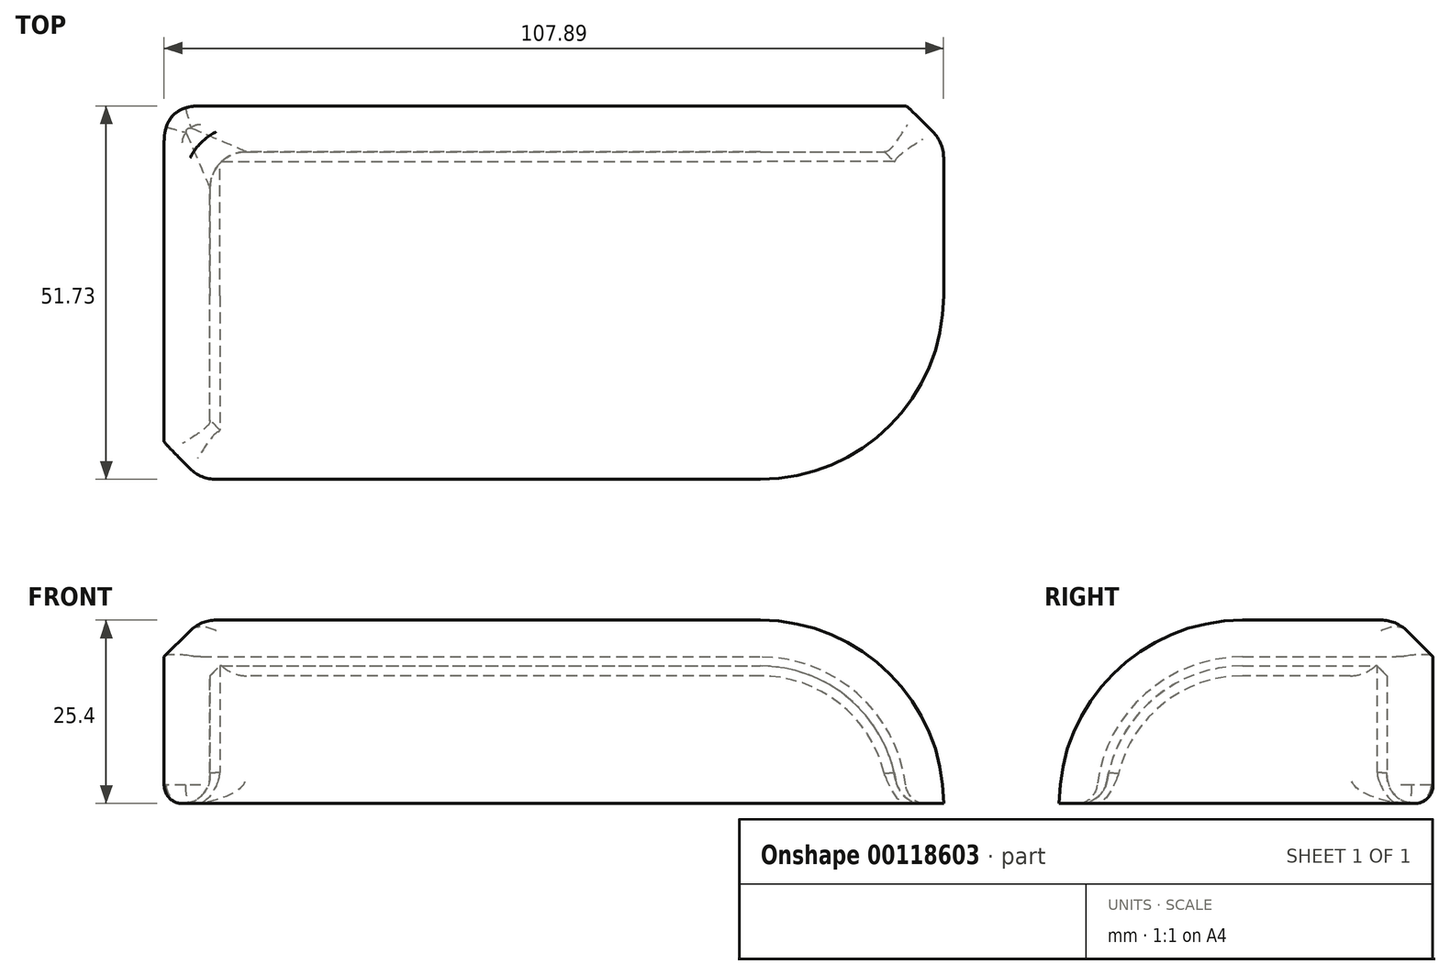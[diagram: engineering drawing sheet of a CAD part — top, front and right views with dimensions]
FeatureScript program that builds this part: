
annotation { "Feature Type Name" : "Feature", "Feature Type Description" : "" }
export const myFeature = defineFeature(function(context is Context, id is Id, definition is map)
    precondition{}
    {
        {
            var Q0;
            Q0=qCreatedBy(makeId("Top.planeOp"),FACE);
            var sketch = newSketch(context, id + "F0", { "sketchPlane" : qUnion([Q0])});
            skLineSegment(sketch, "E0.bottom", {"start": v(-60.63, -3.39) * mm, "end": v(47.26, -3.39) * mm});
            skLineSegment(sketch, "E0.top", {"start": v(-60.63, 48.34) * mm, "end": v(47.26, 48.34) * mm});
            skLineSegment(sketch, "E0.left", {"start": v(-60.63, -3.39) * mm, "end": v(-60.63, 48.34) * mm});
            skLineSegment(sketch, "E0.right", {"start": v(47.26, -3.39) * mm, "end": v(47.26, 48.34) * mm});
            skSolve(sketch);
        }
        {
            var Q0;
            Q0=makeQuery(id+"F0.imprint","IMPRINT",FACE,{"disambiguationData":[TD([[makeQuery(id+"F0.imprint","IMPRINT",EDGE,{"derivedFrom":sQuery(id+"F0.wireOp",EDGE,"E0.bottom")}),1.0]])]});
            extrude(context, id + "F1", {"entities" : qUnion([Q0]), "depth" : 25.4 * mm});
        }
        {
            var Q0;
            Q0=makeQuery(id+"F1.opExtrude","CAP_EDGE",EDGE,{"disambiguationData":[OSD([sQuery(id+"F0.wireOp",EDGE,"E0.bottom")])],"isStart":false});
            var Q1;
            Q1=makeQuery(id+"F1.opExtrude","CAP_EDGE",EDGE,{"disambiguationData":[OSD([sQuery(id+"F0.wireOp",EDGE,"E0.right")])],"isStart":false});
            var Q2;
            Q2=makeQuery(id+"F1.opExtrude","SWEPT_EDGE",EDGE,{"disambiguationData":[OSD([sQuery(id+"F0.wireOp",EDGE,"E0.bottom"),sQuery(id+"F0.wireOp",EDGE,"E0.right")])]});
            fillet(context, id + "F2", {"entities" : qUnion([Q0, Q1, Q2]), "radius" : 25.4 * mm, "tangentPropagation" : true, "allowEdgeOverflow" : false});
        }
        {
            var Q0;
            Q0=makeQuery(id+"F2.opFillet","BLEND_EDGE",EDGE,{"blendedFrom":[makeQuery(id+"F1.opExtrude","CAP_EDGE",EDGE,{"disambiguationData":[OSD([sQuery(id+"F0.wireOp",EDGE,"E0.right")])],"isStart":false}),makeQuery(id+"F1.opExtrude","SWEPT_FACE",FACE,{"disambiguationData":[OSD([sQuery(id+"F0.wireOp",EDGE,"E0.top")])]})],"blendedInto":[makeQuery(id+"F1.opExtrude","SWEPT_FACE",FACE,{"disambiguationData":[OSD([sQuery(id+"F0.wireOp",EDGE,"E0.top")])]})]});
            var Q1;
            Q1=makeQuery(id+"F1.opExtrude","CAP_FACE",FACE,{"disambiguationData":[OSD([sQuery(id+"F0.wireOp",EDGE,"E0.bottom"),sQuery(id+"F0.wireOp",EDGE,"E0.top"),sQuery(id+"F0.wireOp",EDGE,"E0.left"),sQuery(id+"F0.wireOp",EDGE,"E0.right")])],"isStart":false});
            chamfer(context, id + "F3", {"entities" : qUnion([Q0, Q1]), "width" : 5.08 * mm, "tangentPropagation" : true});
        }
        {
            var Q0;
            Q0=makeQuery(id+"F1.opExtrude","CAP_FACE",FACE,{"disambiguationData":[OSD([sQuery(id+"F0.wireOp",EDGE,"E0.bottom"),sQuery(id+"F0.wireOp",EDGE,"E0.top"),sQuery(id+"F0.wireOp",EDGE,"E0.left"),sQuery(id+"F0.wireOp",EDGE,"E0.right")])],"isStart":true});
            shell(context, id + "F4", {"entities" : qUnion([Q0]), "thickness" : 6.35 * mm});
        }
        {
            var Q0;
            {var subQ0=sQuery(id+"F0.wireOp",EDGE,"E0.top");Q0=makeQuery(id+"F4.opShell","OFFSET_EDGE",EDGE,{"disambiguationData":[OSD([subQ0]),TDD([makeQuery(id+"F1.opExtrude","CAP_EDGE",EDGE,{"disambiguationData":[OSD([subQ0])],"isStart":true})])]});}
            var Q1;
            {var subQ0=sQuery(id+"F0.wireOp",EDGE,"E0.right");var subQ1=sQuery(id+"F0.wireOp",EDGE,"E0.left");var subQ2=sQuery(id+"F0.wireOp",EDGE,"E0.top");var subQ3=sQuery(id+"F0.wireOp",EDGE,"E0.bottom");Q1=makeQuery(id+"F4.opShell","OFFSET_EDGE",EDGE,{"disambiguationData":[OSD([subQ3,subQ2,subQ1,subQ0]),TDD([makeQuery(id+"F2.opFillet","BLEND_EDGE",EDGE,{"blendedFrom":[makeQuery(id+"F1.opExtrude","CAP_EDGE",EDGE,{"disambiguationData":[OSD([subQ0])],"isStart":false}),makeQuery(id+"F1.opExtrude","CAP_FACE",FACE,{"disambiguationData":[OSD([subQ3,subQ2,subQ1,subQ0])],"isStart":true})],"blendedInto":[makeQuery(id+"F1.opExtrude","CAP_FACE",FACE,{"disambiguationData":[OSD([subQ3,subQ2,subQ1,subQ0])],"isStart":true})]})])]});}
            var Q2;
            {var subQ0=sQuery(id+"F0.wireOp",EDGE,"E0.left");Q2=makeQuery(id+"F4.opShell","OFFSET_EDGE",EDGE,{"disambiguationData":[OSD([subQ0]),TDD([makeQuery(id+"F1.opExtrude","CAP_EDGE",EDGE,{"disambiguationData":[OSD([subQ0])],"isStart":true})])]});}
            var Q3;
            {var subQ0=sQuery(id+"F0.wireOp",EDGE,"E0.right");var subQ1=sQuery(id+"F0.wireOp",EDGE,"E0.left");var subQ2=sQuery(id+"F0.wireOp",EDGE,"E0.top");var subQ3=sQuery(id+"F0.wireOp",EDGE,"E0.bottom");Q3=makeQuery(id+"F4.opShell","OFFSET_EDGE",EDGE,{"disambiguationData":[OSD([subQ3,subQ2,subQ1,subQ0]),TDD([makeQuery(id+"F2.opFillet","BLEND_EDGE",EDGE,{"blendedFrom":[makeQuery(id+"F1.opExtrude","CAP_VERTEX",VERTEX,{"disambiguationData":[OSD([subQ3,subQ0])],"isStart":false}),makeQuery(id+"F1.opExtrude","CAP_FACE",FACE,{"disambiguationData":[OSD([subQ3,subQ2,subQ1,subQ0])],"isStart":true})],"blendedInto":[makeQuery(id+"F1.opExtrude","CAP_FACE",FACE,{"disambiguationData":[OSD([subQ3,subQ2,subQ1,subQ0])],"isStart":true})]})])]});}
            var Q4;
            {var subQ0=sQuery(id+"F0.wireOp",EDGE,"E0.right");var subQ1=sQuery(id+"F0.wireOp",EDGE,"E0.left");var subQ2=sQuery(id+"F0.wireOp",EDGE,"E0.top");var subQ3=sQuery(id+"F0.wireOp",EDGE,"E0.bottom");Q4=makeQuery(id+"F4.opShell","OFFSET_EDGE",EDGE,{"disambiguationData":[OSD([subQ3,subQ2,subQ1,subQ0]),TDD([makeQuery(id+"F2.opFillet","BLEND_EDGE",EDGE,{"blendedFrom":[makeQuery(id+"F1.opExtrude","CAP_EDGE",EDGE,{"disambiguationData":[OSD([subQ3])],"isStart":false}),makeQuery(id+"F1.opExtrude","CAP_FACE",FACE,{"disambiguationData":[OSD([subQ3,subQ2,subQ1,subQ0])],"isStart":true})],"blendedInto":[makeQuery(id+"F1.opExtrude","CAP_FACE",FACE,{"disambiguationData":[OSD([subQ3,subQ2,subQ1,subQ0])],"isStart":true})]})])]});}
            fillet(context, id + "F5", {"entities" : qUnion([Q0, Q1, Q2, Q3, Q4]), "radius" : 3.8 * mm, "tangentPropagation" : true, "allowEdgeOverflow" : false});
        }
        {
            var Q0;
            {var subQ0=sQuery(id+"F0.wireOp",EDGE,"E0.right");var subQ1=sQuery(id+"F0.wireOp",EDGE,"E0.left");var subQ2=sQuery(id+"F0.wireOp",EDGE,"E0.top");var subQ3=sQuery(id+"F0.wireOp",EDGE,"E0.bottom");Q0=makeQuery(id+"F4.opShell","OFFSET_EDGE",EDGE,{"disambiguationData":[OSD([subQ3,subQ2,subQ1,subQ0]),TDD([makeQuery(id+"F3.opChamfer","BLEND_EDGE",EDGE,{"blendedFrom":[makeQuery(id+"F2.opFillet","BLEND_EDGE",EDGE,{"blendedFrom":[makeQuery(id+"F1.opExtrude","CAP_EDGE",EDGE,{"disambiguationData":[OSD([subQ3])],"isStart":false}),makeQuery(id+"F1.opExtrude","SWEPT_FACE",FACE,{"disambiguationData":[OSD([subQ1])]})],"blendedInto":[makeQuery(id+"F1.opExtrude","SWEPT_FACE",FACE,{"disambiguationData":[OSD([subQ1])]})]}),makeQuery(id+"F1.opExtrude","CAP_FACE",FACE,{"disambiguationData":[OSD([subQ3,subQ2,subQ1,subQ0])],"isStart":true})],"blendedInto":[makeQuery(id+"F1.opExtrude","CAP_FACE",FACE,{"disambiguationData":[OSD([subQ3,subQ2,subQ1,subQ0])],"isStart":true})]})])]});}
            var Q1;
            {var subQ0=sQuery(id+"F0.wireOp",EDGE,"E0.top");var subQ1=sQuery(id+"F0.wireOp",EDGE,"E0.left");Q1=makeQuery(id+"F5.opFillet","BLEND_EDGE",EDGE,{"blendedFrom":[makeQuery(id+"F4.opShell","OFFSET_EDGE",EDGE,{"disambiguationData":[OSD([subQ1]),TDD([makeQuery(id+"F1.opExtrude","CAP_EDGE",EDGE,{"disambiguationData":[OSD([subQ1])],"isStart":true})])]}),makeQuery(id+"F4.opShell","OFFSET_EDGE",EDGE,{"disambiguationData":[OSD([subQ0]),TDD([makeQuery(id+"F1.opExtrude","CAP_EDGE",EDGE,{"disambiguationData":[OSD([subQ0])],"isStart":true})])]})],"blendedInto":[]});}
            var Q2;
            {var subQ0=sQuery(id+"F0.wireOp",EDGE,"E0.right");var subQ1=sQuery(id+"F0.wireOp",EDGE,"E0.left");var subQ2=sQuery(id+"F0.wireOp",EDGE,"E0.top");var subQ3=sQuery(id+"F0.wireOp",EDGE,"E0.bottom");Q2=makeQuery(id+"F4.opShell","OFFSET_EDGE",EDGE,{"disambiguationData":[OSD([subQ3,subQ2,subQ1,subQ0]),TDD([makeQuery(id+"F3.opChamfer","BLEND_EDGE",EDGE,{"blendedFrom":[makeQuery(id+"F2.opFillet","BLEND_EDGE",EDGE,{"blendedFrom":[makeQuery(id+"F1.opExtrude","CAP_EDGE",EDGE,{"disambiguationData":[OSD([subQ0])],"isStart":false}),makeQuery(id+"F1.opExtrude","SWEPT_FACE",FACE,{"disambiguationData":[OSD([subQ2])]})],"blendedInto":[makeQuery(id+"F1.opExtrude","SWEPT_FACE",FACE,{"disambiguationData":[OSD([subQ2])]})]}),makeQuery(id+"F1.opExtrude","CAP_FACE",FACE,{"disambiguationData":[OSD([subQ3,subQ2,subQ1,subQ0])],"isStart":true})],"blendedInto":[makeQuery(id+"F1.opExtrude","CAP_FACE",FACE,{"disambiguationData":[OSD([subQ3,subQ2,subQ1,subQ0])],"isStart":true})]})])]});}
            fillet(context, id + "F6", {"entities" : qUnion([Q0, Q1, Q2]), "radius" : 5.08 * mm, "tangentPropagation" : true, "allowEdgeOverflow" : false});
        }
        {
            var Q0;
            {var subQ0=sQuery(id+"F0.wireOp",EDGE,"E0.right");Q0=makeQuery(id+"F3.opChamfer","BLEND_EDGE",EDGE,{"blendedFrom":[makeQuery(id+"F2.opFillet","BLEND_EDGE",EDGE,{"blendedFrom":[makeQuery(id+"F1.opExtrude","CAP_EDGE",EDGE,{"disambiguationData":[OSD([subQ0])],"isStart":false}),makeQuery(id+"F1.opExtrude","SWEPT_FACE",FACE,{"disambiguationData":[OSD([sQuery(id+"F0.wireOp",EDGE,"E0.top")])]})],"blendedInto":[makeQuery(id+"F1.opExtrude","SWEPT_FACE",FACE,{"disambiguationData":[OSD([sQuery(id+"F0.wireOp",EDGE,"E0.top")])]})]}),makeQuery(id+"F2.opFillet","BLEND_FACE",FACE,{"disambiguationData":[OSD([subQ0])]})],"blendedInto":[makeQuery(id+"F2.opFillet","BLEND_FACE",FACE,{"disambiguationData":[OSD([subQ0])]})]});}
            var Q1;
            {var subQ0=sQuery(id+"F0.wireOp",EDGE,"E0.top");Q1=makeQuery(id+"F3.opChamfer","BLEND_EDGE",EDGE,{"blendedFrom":[makeQuery(id+"F1.opExtrude","CAP_EDGE",EDGE,{"disambiguationData":[OSD([subQ0])],"isStart":false}),makeQuery(id+"F1.opExtrude","CAP_FACE",FACE,{"disambiguationData":[OSD([sQuery(id+"F0.wireOp",EDGE,"E0.bottom"),subQ0,sQuery(id+"F0.wireOp",EDGE,"E0.left"),sQuery(id+"F0.wireOp",EDGE,"E0.right")])],"isStart":false})],"blendedInto":[makeQuery(id+"F1.opExtrude","CAP_FACE",FACE,{"disambiguationData":[OSD([sQuery(id+"F0.wireOp",EDGE,"E0.bottom"),subQ0,sQuery(id+"F0.wireOp",EDGE,"E0.left"),sQuery(id+"F0.wireOp",EDGE,"E0.right")])],"isStart":false})]});}
            var Q2;
            {var subQ0=sQuery(id+"F0.wireOp",EDGE,"E0.bottom");Q2=makeQuery(id+"F3.opChamfer","BLEND_EDGE",EDGE,{"blendedFrom":[makeQuery(id+"F2.opFillet","BLEND_EDGE",EDGE,{"blendedFrom":[makeQuery(id+"F1.opExtrude","CAP_EDGE",EDGE,{"disambiguationData":[OSD([subQ0])],"isStart":false}),makeQuery(id+"F1.opExtrude","SWEPT_FACE",FACE,{"disambiguationData":[OSD([sQuery(id+"F0.wireOp",EDGE,"E0.left")])]})],"blendedInto":[makeQuery(id+"F1.opExtrude","SWEPT_FACE",FACE,{"disambiguationData":[OSD([sQuery(id+"F0.wireOp",EDGE,"E0.left")])]})]}),makeQuery(id+"F2.opFillet","BLEND_FACE",FACE,{"disambiguationData":[OSD([subQ0])]})],"blendedInto":[makeQuery(id+"F2.opFillet","BLEND_FACE",FACE,{"disambiguationData":[OSD([subQ0])]})]});}
            var Q3;
            {var subQ0=sQuery(id+"F0.wireOp",EDGE,"E0.left");Q3=makeQuery(id+"F3.opChamfer","BLEND_EDGE",EDGE,{"blendedFrom":[makeQuery(id+"F1.opExtrude","CAP_EDGE",EDGE,{"disambiguationData":[OSD([subQ0])],"isStart":false}),makeQuery(id+"F1.opExtrude","CAP_FACE",FACE,{"disambiguationData":[OSD([sQuery(id+"F0.wireOp",EDGE,"E0.bottom"),sQuery(id+"F0.wireOp",EDGE,"E0.top"),subQ0,sQuery(id+"F0.wireOp",EDGE,"E0.right")])],"isStart":false})],"blendedInto":[makeQuery(id+"F1.opExtrude","CAP_FACE",FACE,{"disambiguationData":[OSD([sQuery(id+"F0.wireOp",EDGE,"E0.bottom"),sQuery(id+"F0.wireOp",EDGE,"E0.top"),subQ0,sQuery(id+"F0.wireOp",EDGE,"E0.right")])],"isStart":false})]});}
            var Q4;
            Q4=makeQuery(id+"F3.opChamfer","BLEND_EDGE",EDGE,{"blendedFrom":[makeQuery(id+"F1.opExtrude","CAP_EDGE",EDGE,{"disambiguationData":[OSD([sQuery(id+"F0.wireOp",EDGE,"E0.left")])],"isStart":false}),makeQuery(id+"F1.opExtrude","CAP_EDGE",EDGE,{"disambiguationData":[OSD([sQuery(id+"F0.wireOp",EDGE,"E0.top")])],"isStart":false})],"blendedInto":[]});
            fillet(context, id + "F7", {"entities" : qUnion([Q0, Q1, Q2, Q3, Q4]), "radius" : 5.08 * mm, "tangentPropagation" : true, "allowEdgeOverflow" : false});
        }
        {
            var Q0;
            Q0=makeQuery(id+"F1.opExtrude","SWEPT_EDGE",EDGE,{"disambiguationData":[OSD([sQuery(id+"F0.wireOp",EDGE,"E0.top"),sQuery(id+"F0.wireOp",EDGE,"E0.left")])]});
            fillet(context, id + "F8", {"entities" : qUnion([Q0]), "radius" : 5.08 * mm, "tangentPropagation" : true, "rho" : 0.5, "crossSection" : FilletCrossSection.CONIC, "allowEdgeOverflow" : false});
        }
        {
            var Q0;
            Q0=makeQuery(id+"F1.opExtrude","CAP_EDGE",EDGE,{"disambiguationData":[OSD([sQuery(id+"F0.wireOp",EDGE,"E0.top")])],"isStart":true});
            var Q1;
            {var subQ0=sQuery(id+"F0.wireOp",EDGE,"E0.left");var subQ1=sQuery(id+"F0.wireOp",EDGE,"E0.top");Q1=makeQuery(id+"F8.opFillet","BLEND_EDGE",EDGE,{"blendedFrom":[makeQuery(id+"F1.opExtrude","SWEPT_EDGE",EDGE,{"disambiguationData":[OSD([subQ1,subQ0])]}),makeQuery(id+"F1.opExtrude","CAP_FACE",FACE,{"disambiguationData":[OSD([sQuery(id+"F0.wireOp",EDGE,"E0.bottom"),subQ1,subQ0,sQuery(id+"F0.wireOp",EDGE,"E0.right")])],"isStart":true})],"blendedInto":[makeQuery(id+"F1.opExtrude","CAP_FACE",FACE,{"disambiguationData":[OSD([sQuery(id+"F0.wireOp",EDGE,"E0.bottom"),subQ1,subQ0,sQuery(id+"F0.wireOp",EDGE,"E0.right")])],"isStart":true})]});}
            fillet(context, id + "F9", {"entities" : qUnion([Q0, Q1]), "radius" : 2.54 * mm, "tangentPropagation" : true, "allowEdgeOverflow" : false});
        }
    });
